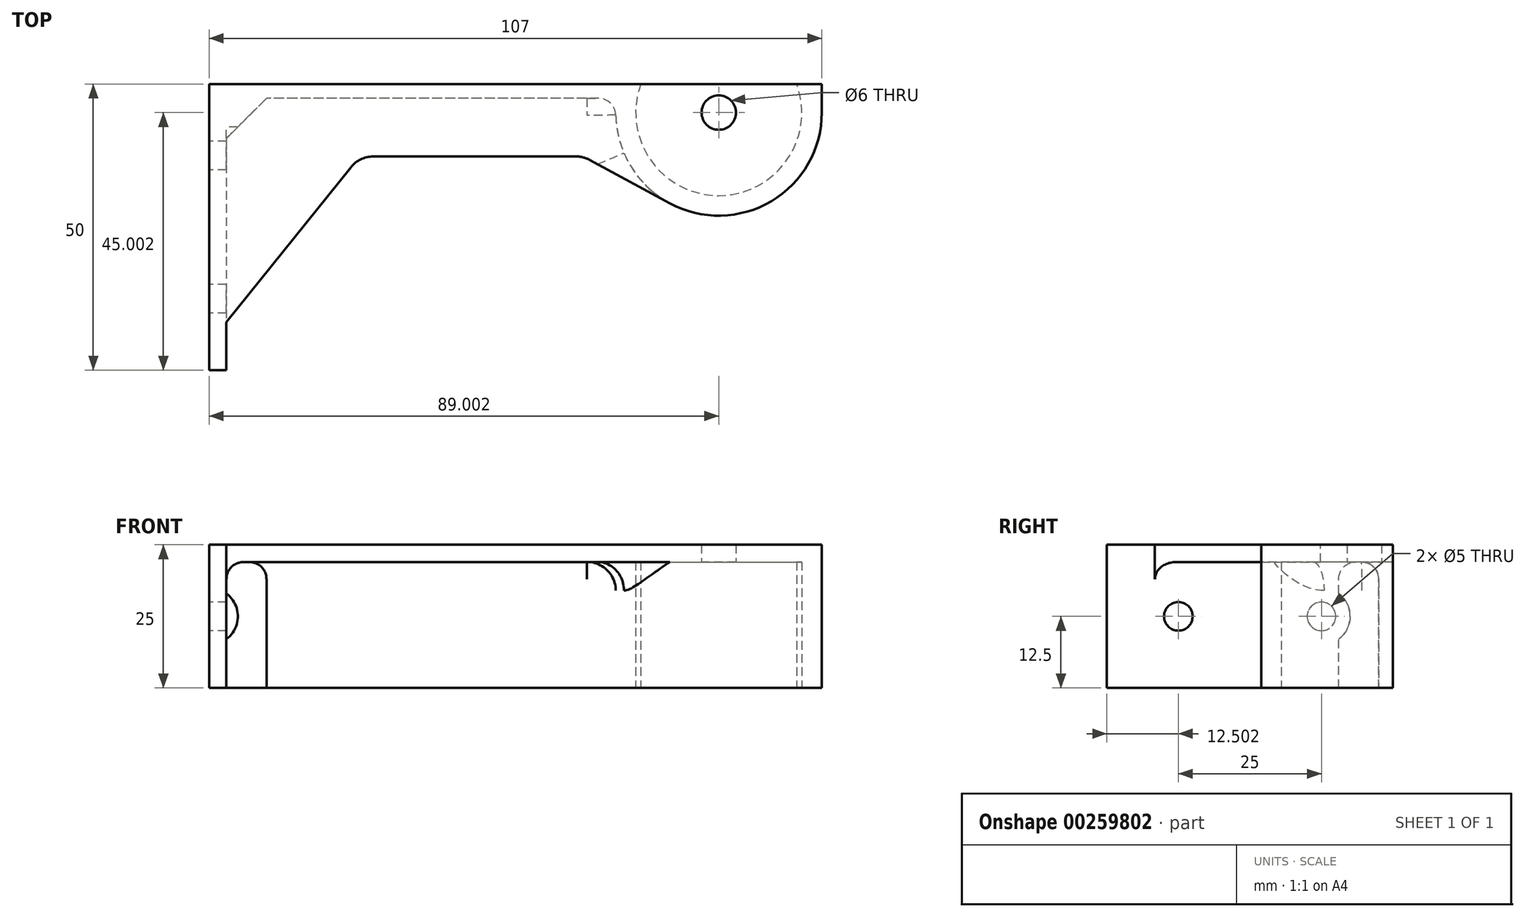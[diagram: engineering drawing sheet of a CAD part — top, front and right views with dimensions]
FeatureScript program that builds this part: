
annotation { "Feature Type Name" : "Feature", "Feature Type Description" : "" }
export const myFeature = defineFeature(function(context is Context, id is Id, definition is map)
    precondition{}
    {
        {
            var Q0;
            Q0=qCreatedBy(makeId("Top.planeOp"),FACE);
            var sketch = newSketch(context, id + "F0", { "sketchPlane" : qUnion([Q0])});
            skLineSegment(sketch, "E0", {"start": v(-44.26, -25.47) * mm, "end": v(-44.26, 24.53) * mm});
            skLineSegment(sketch, "E1", {"start": v(-44.26, 24.53) * mm, "end": v(62.74, 24.53) * mm});
            skCircle(sketch, "E2", {"center": v(44.74, 19.53) * mm, "radius": 3 * mm});
            skArc(sketch, "E3", {"start": v(26.74, 19.53) * mm, "mid": v(44.74, 1.53) * mm, "end": v(62.74, 19.53) * mm});
            skLineSegment(sketch, "E4", {"start": v(18.42, 19.53) * mm, "end": v(70.29, 19.53) * mm, "construction": true});
            skLineSegment(sketch, "E5", {"start": v(26.74, 19.53) * mm, "end": v(26.74, 22.03) * mm});
            skLineSegment(sketch, "E6", {"start": v(62.74, 19.53) * mm, "end": v(62.74, 24.53) * mm});
            skLineSegment(sketch, "E7", {"start": v(26.74, 22.03) * mm, "end": v(-41.26, 22.03) * mm});
            skLineSegment(sketch, "E8", {"start": v(-41.26, 22.03) * mm, "end": v(-41.26, -25.47) * mm});
            skPoint(sketch, "E9.orphan", {"position": v(26.74, 24.53) * mm});
            skLineSegment(sketch, "E10", {"start": v(-44.26, -25.47) * mm, "end": v(-41.26, -25.47) * mm});
            skArc(sketch, "E11", {"start": v(31.13, 24.53) * mm, "mid": v(44.74, 5.03) * mm, "end": v(58.35, 24.53) * mm});
            skSolve(sketch);
        }
        {
            var Q0;
            {var subQ3=sQuery(id+"F0.wireOp",EDGE,"E0");Q0=makeQuery(id+"F0.imprint","IMPRINT",FACE,{"disambiguationData":[TD([[makeQuery(id+"F0.imprint","IMPRINT",EDGE,{"derivedFrom":subQ3}),-1.0]])]});}
            extrude(context, id + "F1", {"entities" : qUnion([Q0]), "depth" : 25 * mm, "offsetDistance" : 25 * mm});
        }
        {
            var Q0;
            Q0=makeQuery(id+"F1.opExtrude","CAP_FACE",FACE,{"disambiguationData":[OSD([sQuery(id+"F0.wireOp",EDGE,"E0"),sQuery(id+"F0.wireOp",EDGE,"E1"),sQuery(id+"F0.wireOp",EDGE,"8QMgwL4l-eUgF-bXba-84mB-vObHb4zvUH5H"),sQuery(id+"F0.wireOp",EDGE,"E3"),sQuery(id+"F0.wireOp",EDGE,"E5"),sQuery(id+"F0.wireOp",EDGE,"P25SQ9gr-SBM6-nuFK-kGic-qiJolmAvlV25"),sQuery(id+"F0.wireOp",EDGE,"jLxib0JA-VgGV-74Fc-wNGU-5bSYWisP3I0S"),sQuery(id+"F0.wireOp",EDGE,"E6"),sQuery(id+"F0.wireOp",EDGE,"E7"),sQuery(id+"F0.wireOp",EDGE,"E8"),sQuery(id+"F0.wireOp",EDGE,"E10")])],"isStart":false});
            var sketch = newSketch(context, id + "F2", { "sketchPlane" : qUnion([Q0])});
            skLineSegment(sketch, "E12", {"start": v(36.18, 3.7) * mm, "end": v(22.2, 11.26) * mm});
            skLineSegment(sketch, "E13", {"start": v(-41.26, -17.06) * mm, "end": v(-19.5, 10) * mm});
            skLineSegment(sketch, "E14", {"start": v(-15.6, 11.87) * mm, "end": v(19.82, 11.87) * mm});
            skPoint(sketch, "E15.visualSharp", {"position": v(21.09, 11.87) * mm});
            skArc(sketch, "E15.filletArc", {"start": v(22.2, 11.26) * mm, "mid": v(21.05, 11.71) * mm, "end": v(19.82, 11.87) * mm});
            skPoint(sketch, "E16.visualSharp", {"position": v(-18, 11.87) * mm});
            skArc(sketch, "E16.filletArc", {"start": v(-15.6, 11.87) * mm, "mid": v(-17.77, 11.38) * mm, "end": v(-19.5, 10) * mm});
            skLineSegment(sketch, "E17", {"start": v(31.13, 24.53) * mm, "end": v(58.35, 24.53) * mm});
            skSolve(sketch);
        }
        {
            var Q0;
            {var subQ7=sQuery(id+"F0.wireOp",EDGE,"E0");Q0=makeQuery(id+"F2.imprint","IMPRINT",FACE,{"disambiguationData":[TD([[makeQuery(id+"F2.imprint","IMPRINT",EDGE,{"derivedFrom":makeQuery(id+"F1.opExtrude","CAP_EDGE",EDGE,{"disambiguationData":[OSD([subQ7])],"isStart":false})}),-1.0]])]});}
            var Q1;
            {var subQ2=sQuery(id+"F2.wireOp",EDGE,"E12");Q1=makeQuery(id+"F2.imprint","IMPRINT",FACE,{"disambiguationData":[TD([[makeQuery(id+"F2.imprint","IMPRINT",EDGE,{"derivedFrom":subQ2}),-1.0]])]});}
            var Q2;
            Q2=makeQuery(id+"F2.imprint","IMPRINT",FACE,{"disambiguationData":[TD([[makeQuery(id+"F2.imprint","IMPRINT",EDGE,{"derivedFrom":sQuery(id+"F2.wireOp",EDGE,"E17")}),-1.0]])]});
            extrude(context, id + "F3", {"entities" : qUnion([Q0, Q1, Q2]), "operationType" : NewBodyOperationType.ADD, "oppositeDirection" : true, "depth" : 3 * mm, "offsetDistance" : 25 * mm});
        }
        {
            var Q0;
            Q0=makeQuery(id+"F1.opExtrude","SWEPT_FACE",FACE,{"disambiguationData":[OSD([sQuery(id+"F0.wireOp",EDGE,"E0")])]});
            var sketch = newSketch(context, id + "F4", { "sketchPlane" : qUnion([Q0])});
            skCircle(sketch, "E18", {"center": v(-12.03, 12.5) * mm, "radius": 2.5 * mm});
            skCircle(sketch, "E19", {"center": v(12.97, 12.5) * mm, "radius": 2.5 * mm});
            skSolve(sketch);
        }
        {
            var Q0;
            Q0=makeQuery(id+"F4.imprint","IMPRINT",FACE,{"disambiguationData":[TD([[makeQuery(id+"F4.imprint","IMPRINT",EDGE,{"derivedFrom":sQuery(id+"F4.wireOp",EDGE,"E19")}),1.0]])]});
            var Q1;
            Q1=makeQuery(id+"F4.imprint","IMPRINT",FACE,{"disambiguationData":[TD([[makeQuery(id+"F4.imprint","IMPRINT",EDGE,{"derivedFrom":sQuery(id+"F4.wireOp",EDGE,"E18")}),1.0]])]});
            var Q2;
            Q2=sQuery(id+"F4.wireOp",EDGE,"E18");
            var Q3;
            Q3=sQuery(id+"F4.wireOp",EDGE,"E19");
            extrude(context, id + "F5", {"entities" : qUnion([Q0, Q1]), "operationType" : NewBodyOperationType.REMOVE, "surfaceEntities" : qUnion([Q2, Q3]), "oppositeDirection" : true, "depth" : 25 * mm, "offsetDistance" : 25 * mm});
        }
        {
            var Q0;
            Q0=makeQuery(id+"F0.imprint","IMPRINT",FACE,{"disambiguationData":[TD([[makeQuery(id+"F0.imprint","IMPRINT",EDGE,{"derivedFrom":sQuery(id+"F0.wireOp",EDGE,"E2")}),1.0]])]});
            var Q1;
            Q1=sQuery(id+"F0.wireOp",EDGE,"E2");
            extrude(context, id + "F6", {"entities" : qUnion([Q0]), "operationType" : NewBodyOperationType.REMOVE, "surfaceEntities" : qUnion([Q1]), "depth" : 30 * mm, "offsetDistance" : 25 * mm});
        }
        {
            var Q0;
            {var subQ0=sQuery(id+"F0.wireOp",EDGE,"E8");var subQ1=sQuery(id+"F2.wireOp",EDGE,"E15.filletArc");var subQ2=sQuery(id+"F0.wireOp",EDGE,"E3");var subQ3=sQuery(id+"F2.wireOp",EDGE,"E14");var subQ4=sQuery(id+"F2.wireOp",EDGE,"E12");var subQ5=sQuery(id+"F2.wireOp",EDGE,"E13");var subQ6=sQuery(id+"F2.wireOp",EDGE,"E16.filletArc");Q0=makeQuery(id+"F3.boolean.opBoolean","SPLIT",FACE,{"disambiguationData":[TD([makeQuery(id+"F1.opExtrude","SWEPT_FACE",FACE,{"disambiguationData":[OSD([subQ2])]})])],"derivedFrom":makeQuery(id+"F3.opExtrude","CAP_FACE",FACE,{"disambiguationData":[OSD([sQuery(id+"F0.wireOp",EDGE,"E0"),sQuery(id+"F0.wireOp",EDGE,"E1"),subQ2,sQuery(id+"F0.wireOp",EDGE,"E6"),subQ0,sQuery(id+"F0.wireOp",EDGE,"E10"),subQ4,subQ5,subQ3,subQ1,subQ6,sQuery(id+"F2.wireOp",EDGE,"E17")])],"isStart":false})});}
            var sketch = newSketch(context, id + "F7", { "sketchPlane" : qUnion([Q0])});
            skLineSegment(sketch, "E20", {"start": v(-41.26, -22.03) * mm, "end": v(-34.26, -22.03) * mm});
            skLineSegment(sketch, "E21", {"start": v(-34.26, -22.03) * mm, "end": v(-41.26, -15.03) * mm});
            skSolve(sketch);
        }
        {
            var Q0;
            {var subQ0=sQuery(id+"F7.wireOp",EDGE,"E20");Q0=makeQuery(id+"F7.imprint","IMPRINT",FACE,{"disambiguationData":[TD([[makeQuery(id+"F7.imprint","IMPRINT",EDGE,{"derivedFrom":subQ0}),-1.0]])]});}
            extrude(context, id + "F8", {"entities" : qUnion([Q0]), "operationType" : NewBodyOperationType.ADD, "depth" : 22 * mm, "offsetDistance" : 25 * mm});
        }
        {
            var Q0;
            Q0=makeQuery(id+"F1.opExtrude","SWEPT_FACE",FACE,{"disambiguationData":[OSD([sQuery(id+"F0.wireOp",EDGE,"E8")])]});
            var sketch = newSketch(context, id + "F9", { "sketchPlane" : qUnion([Q0])});
            skCircle(sketch, "E22", {"center": v(12.03, 12.5) * mm, "radius": 5 * mm});
            skSolve(sketch);
        }
        {
            var Q0;
            Q0=makeQuery(id+"F9.imprint","IMPRINT",FACE,{"disambiguationData":[TD([[makeQuery(id+"F9.imprint","IMPRINT",EDGE,{"derivedFrom":sQuery(id+"F9.wireOp",EDGE,"E22")}),1.0]])]});
            extrude(context, id + "F10", {"entities" : qUnion([Q0]), "operationType" : NewBodyOperationType.REMOVE, "depth" : 25 * mm, "offsetDistance" : 25 * mm});
        }
        {
            var Q0;
            Q0=makeQuery(id+"F8.opExtrude","SWEPT_EDGE",EDGE,{"disambiguationData":[OSD([sQuery(id+"F0.wireOp",EDGE,"E0"),sQuery(id+"F0.wireOp",EDGE,"E1"),sQuery(id+"F0.wireOp",EDGE,"E3"),sQuery(id+"F0.wireOp",EDGE,"E6"),sQuery(id+"F0.wireOp",EDGE,"E7"),sQuery(id+"F0.wireOp",EDGE,"E8"),sQuery(id+"F0.wireOp",EDGE,"E10"),sQuery(id+"F2.wireOp",EDGE,"E12"),sQuery(id+"F2.wireOp",EDGE,"E13"),sQuery(id+"F2.wireOp",EDGE,"E14"),sQuery(id+"F2.wireOp",EDGE,"E15.filletArc"),sQuery(id+"F2.wireOp",EDGE,"E16.filletArc"),sQuery(id+"F2.wireOp",EDGE,"E17"),sQuery(id+"F7.wireOp",EDGE,"E20"),sQuery(id+"F7.wireOp",EDGE,"E21")])]});
            var Q1;
            Q1=makeQuery(id+"F8.opExtrude","CAP_EDGE",EDGE,{"disambiguationData":[OSD([sQuery(id+"F7.wireOp",EDGE,"E21")])],"isStart":true});
            var Q2;
            Q2=makeQuery(id+"F3.boolean.opBoolean","INTERSECT",EDGE,{"derivedFrom":[makeQuery(id+"F1.opExtrude","SWEPT_FACE",FACE,{"disambiguationData":[OSD([sQuery(id+"F0.wireOp",EDGE,"E7")])]}),makeQuery(id+"F3.opExtrude","CAP_FACE",FACE,{"disambiguationData":[OSD([sQuery(id+"F0.wireOp",EDGE,"E0"),sQuery(id+"F0.wireOp",EDGE,"E1"),sQuery(id+"F0.wireOp",EDGE,"E3"),sQuery(id+"F0.wireOp",EDGE,"E6"),sQuery(id+"F0.wireOp",EDGE,"E8"),sQuery(id+"F0.wireOp",EDGE,"E10"),sQuery(id+"F2.wireOp",EDGE,"E12"),sQuery(id+"F2.wireOp",EDGE,"E13"),sQuery(id+"F2.wireOp",EDGE,"E14"),sQuery(id+"F2.wireOp",EDGE,"E15.filletArc"),sQuery(id+"F2.wireOp",EDGE,"E16.filletArc"),sQuery(id+"F2.wireOp",EDGE,"E17")])],"isStart":false})]});
            var Q3;
            {var subQ1=sQuery(id+"F7.wireOp",EDGE,"E21");var subQ2=sQuery(id+"F2.wireOp",EDGE,"E17");var subQ3=sQuery(id+"F2.wireOp",EDGE,"E16.filletArc");var subQ4=sQuery(id+"F2.wireOp",EDGE,"E15.filletArc");var subQ5=sQuery(id+"F2.wireOp",EDGE,"E14");var subQ6=sQuery(id+"F2.wireOp",EDGE,"E13");var subQ7=sQuery(id+"F2.wireOp",EDGE,"E12");var subQ8=sQuery(id+"F0.wireOp",EDGE,"E10");var subQ9=sQuery(id+"F0.wireOp",EDGE,"E8");var subQ10=sQuery(id+"F0.wireOp",EDGE,"E6");var subQ11=sQuery(id+"F0.wireOp",EDGE,"E3");var subQ12=sQuery(id+"F0.wireOp",EDGE,"E1");var subQ13=sQuery(id+"F0.wireOp",EDGE,"E0");Q3=makeQuery(id+"F10.boolean.opBoolean","SPLIT",EDGE,{"disambiguationData":[TD([makeQuery(id+"F3.opExtrude","CAP_FACE",FACE,{"disambiguationData":[OSD([subQ13,subQ12,subQ11,subQ10,subQ9,subQ8,subQ7,subQ6,subQ5,subQ4,subQ3,subQ2])],"isStart":false})])],"derivedFrom":makeQuery(id+"F8.opExtrude","SWEPT_EDGE",EDGE,{"disambiguationData":[OSD([subQ13,subQ12,subQ11,subQ10,subQ9,subQ8,subQ7,subQ6,subQ5,subQ4,subQ3,subQ2,subQ1])]})});}
            var Q4;
            {var subQ0=sQuery(id+"F7.wireOp",EDGE,"E21");var subQ1=sQuery(id+"F0.wireOp",EDGE,"E8");var subQ2=sQuery(id+"F2.wireOp",EDGE,"E17");var subQ3=sQuery(id+"F2.wireOp",EDGE,"E16.filletArc");var subQ4=sQuery(id+"F2.wireOp",EDGE,"E15.filletArc");var subQ5=sQuery(id+"F2.wireOp",EDGE,"E14");var subQ6=sQuery(id+"F2.wireOp",EDGE,"E13");var subQ7=sQuery(id+"F2.wireOp",EDGE,"E12");var subQ8=sQuery(id+"F0.wireOp",EDGE,"E10");var subQ9=sQuery(id+"F0.wireOp",EDGE,"E6");var subQ10=sQuery(id+"F0.wireOp",EDGE,"E3");var subQ11=sQuery(id+"F0.wireOp",EDGE,"E1");var subQ12=sQuery(id+"F0.wireOp",EDGE,"E0");Q4=makeQuery(id+"F10.boolean.opBoolean","SPLIT",EDGE,{"disambiguationData":[TD([makeQuery(id+"F1.opExtrude","CAP_FACE",FACE,{"disambiguationData":[OSD([subQ12,subQ11,subQ10,sQuery(id+"F0.wireOp",EDGE,"E5"),subQ9,sQuery(id+"F0.wireOp",EDGE,"E7"),subQ1,subQ8,sQuery(id+"F0.wireOp",EDGE,"E11")])],"isStart":true})])],"derivedFrom":makeQuery(id+"F8.opExtrude","SWEPT_EDGE",EDGE,{"disambiguationData":[OSD([subQ12,subQ11,subQ10,subQ9,subQ1,subQ8,subQ7,subQ6,subQ5,subQ4,subQ3,subQ2,subQ0])]})});}
            var Q5;
            {var subQ0=sQuery(id+"F0.wireOp",EDGE,"E8");Q5=makeQuery(id+"F3.boolean.opBoolean","INTERSECT",EDGE,{"derivedFrom":[makeQuery(id+"F1.opExtrude","SWEPT_FACE",FACE,{"disambiguationData":[OSD([subQ0])]}),makeQuery(id+"F3.opExtrude","CAP_FACE",FACE,{"disambiguationData":[OSD([sQuery(id+"F0.wireOp",EDGE,"E0"),sQuery(id+"F0.wireOp",EDGE,"E1"),sQuery(id+"F0.wireOp",EDGE,"E3"),sQuery(id+"F0.wireOp",EDGE,"E6"),subQ0,sQuery(id+"F0.wireOp",EDGE,"E10"),sQuery(id+"F2.wireOp",EDGE,"E12"),sQuery(id+"F2.wireOp",EDGE,"E13"),sQuery(id+"F2.wireOp",EDGE,"E14"),sQuery(id+"F2.wireOp",EDGE,"E15.filletArc"),sQuery(id+"F2.wireOp",EDGE,"E16.filletArc"),sQuery(id+"F2.wireOp",EDGE,"E17")])],"isStart":false})]});}
            var Q6;
            Q6=makeQuery(id+"F1.opExtrude","SWEPT_EDGE",EDGE,{"disambiguationData":[OSD([sQuery(id+"F0.wireOp",EDGE,"E5"),sQuery(id+"F0.wireOp",EDGE,"E7")])]});
            fillet(context, id + "F11", {"entities" : qUnion([Q0, Q1, Q2, Q3, Q4, Q5, Q6]), "radius" : 3 * mm, "tangentPropagation" : true, "allowEdgeOverflow" : false});
        }
        {
            var Q0;
            {var subQ0=sQuery(id+"F0.wireOp",EDGE,"E3");Q0=makeQuery(id+"F3.boolean.opBoolean","INTERSECT",EDGE,{"derivedFrom":[makeQuery(id+"F1.opExtrude","SWEPT_FACE",FACE,{"disambiguationData":[OSD([subQ0])]}),makeQuery(id+"F3.opExtrude","CAP_FACE",FACE,{"disambiguationData":[OSD([sQuery(id+"F0.wireOp",EDGE,"E0"),sQuery(id+"F0.wireOp",EDGE,"E1"),subQ0,sQuery(id+"F0.wireOp",EDGE,"E6"),sQuery(id+"F0.wireOp",EDGE,"E8"),sQuery(id+"F0.wireOp",EDGE,"E10"),sQuery(id+"F2.wireOp",EDGE,"E12"),sQuery(id+"F2.wireOp",EDGE,"E13"),sQuery(id+"F2.wireOp",EDGE,"E14"),sQuery(id+"F2.wireOp",EDGE,"E15.filletArc"),sQuery(id+"F2.wireOp",EDGE,"E16.filletArc"),sQuery(id+"F2.wireOp",EDGE,"E17")])],"isStart":false})]});}
            fillet(context, id + "F12", {"entities" : qUnion([Q0]), "radius" : 5 * mm, "tangentPropagation" : true, "allowEdgeOverflow" : false});
        }
    });
